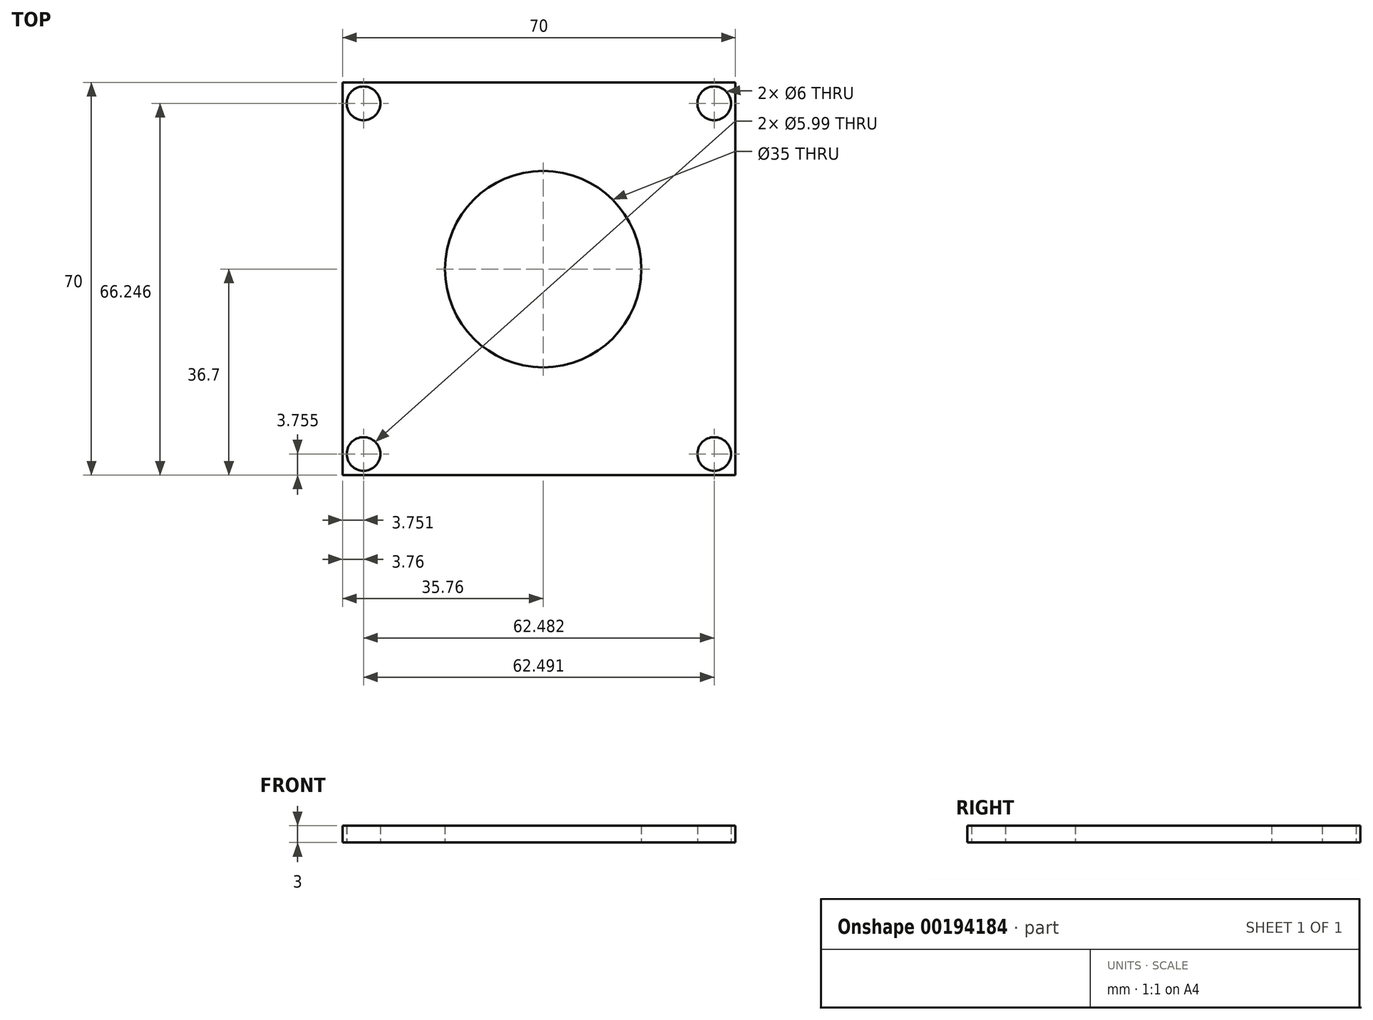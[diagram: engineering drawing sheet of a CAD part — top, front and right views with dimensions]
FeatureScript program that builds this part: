
annotation { "Feature Type Name" : "Feature", "Feature Type Description" : "" }
export const myFeature = defineFeature(function(context is Context, id is Id, definition is map)
    precondition{}
    {
        {
            var Q0;
            Q0=qCreatedBy(makeId("Top.planeOp"),FACE);
            var sketch = newSketch(context, id + "F0", { "sketchPlane" : qUnion([Q0])});
            skLineSegment(sketch, "E0.bottom", {"start": v(-35.76, 33.3) * mm, "end": v(34.24, 33.3) * mm});
            skLineSegment(sketch, "E0.top", {"start": v(-35.76, -36.7) * mm, "end": v(34.24, -36.7) * mm});
            skLineSegment(sketch, "E0.left", {"start": v(-35.76, 33.3) * mm, "end": v(-35.76, -36.7) * mm});
            skLineSegment(sketch, "E0.right", {"start": v(34.24, 33.3) * mm, "end": v(34.24, -36.7) * mm});
            skCircle(sketch, "E1", {"center": v(0, 0) * mm, "radius": 17.5 * mm});
            skCircle(sketch, "E2", {"center": v(-32, 29.55) * mm, "radius": 3 * mm});
            skCircle(sketch, "E3", {"center": v(30.48, 29.55) * mm, "radius": 3 * mm});
            skCircle(sketch, "E4", {"center": v(-32, -32.95) * mm, "radius": 3 * mm});
            skCircle(sketch, "E5", {"center": v(30.48, -32.95) * mm, "radius": 3 * mm});
            skSolve(sketch);
        }
        {
            var Q0;
            Q0=qSketchRegion(id+"F0",true);
            extrude(context, id + "F1", {"entities" : qUnion([Q0]), "depth" : 3 * mm});
        }
    });
